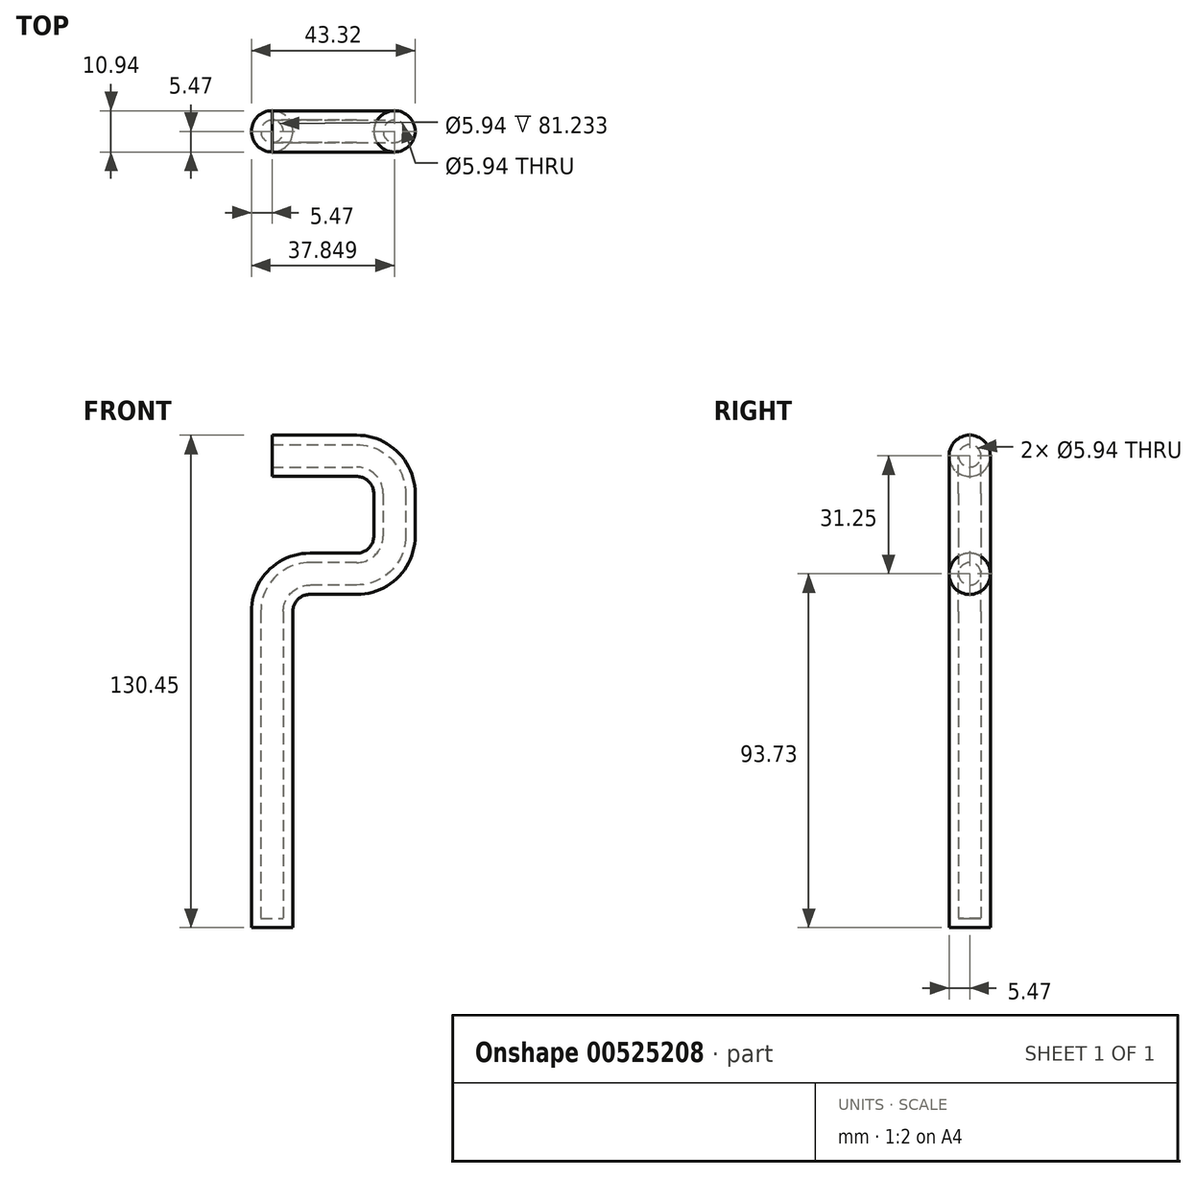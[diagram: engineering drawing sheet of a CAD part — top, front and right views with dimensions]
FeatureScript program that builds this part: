
annotation { "Feature Type Name" : "Feature", "Feature Type Description" : "" }
export const myFeature = defineFeature(function(context is Context, id is Id, definition is map)
    precondition{}
    {
        {
            var Q0;
            Q0=qCreatedBy(makeId("Front.planeOp"),FACE);
            var sketch = newSketch(context, id + "F0", { "sketchPlane" : qUnion([Q0])});
            skLineSegment(sketch, "E0", {"start": v(0, 0) * mm, "end": v(22.38, 0) * mm});
            skLineSegment(sketch, "E1", {"start": v(32.38, -10) * mm, "end": v(32.38, -21.25) * mm});
            skLineSegment(sketch, "E2", {"start": v(22.38, -31.25) * mm, "end": v(10, -31.25) * mm});
            skLineSegment(sketch, "E3", {"start": v(0, -124.98) * mm, "end": v(0, -41.25) * mm});
            skPoint(sketch, "E4.visualSharp", {"position": v(32.38, 0) * mm});
            skArc(sketch, "E4.filletArc", {"start": v(32.38, -10) * mm, "mid": v(29.45, -2.93) * mm, "end": v(22.38, 0) * mm});
            skPoint(sketch, "E5.visualSharp", {"position": v(32.38, -31.25) * mm});
            skArc(sketch, "E5.filletArc", {"start": v(22.38, -31.25) * mm, "mid": v(29.45, -28.32) * mm, "end": v(32.38, -21.25) * mm});
            skPoint(sketch, "E6.visualSharp", {"position": v(0, -31.25) * mm});
            skArc(sketch, "E6.filletArc", {"start": v(10, -31.25) * mm, "mid": v(2.93, -34.18) * mm, "end": v(0, -41.25) * mm});
            skSolve(sketch);
        }
        {
            var Q0;
            Q0=qCreatedBy(makeId("Right.planeOp"),FACE);
            var sketch = newSketch(context, id + "F1", { "sketchPlane" : qUnion([Q0])});
            skCircle(sketch, "E7", {"center": v(0, 0) * mm, "radius": 5.47 * mm});
            skSolve(sketch);
        }
        {
            var Q0;
            Q0=makeQuery(id+"F1.imprint","IMPRINT",FACE,{"disambiguationData":[TD([[makeQuery(id+"F1.imprint","IMPRINT",EDGE,{"derivedFrom":sQuery(id+"F1.wireOp",EDGE,"E7")}),1.0]])]});
            var Q1;
            Q1=sQuery(id+"F0.wireOp",EDGE,"E0");
            var Q2;
            Q2=sQuery(id+"F0.wireOp",EDGE,"E4.filletArc");
            var Q3;
            Q3=sQuery(id+"F0.wireOp",EDGE,"E1");
            var Q4;
            Q4=sQuery(id+"F0.wireOp",EDGE,"E5.filletArc");
            var Q5;
            Q5=sQuery(id+"F0.wireOp",EDGE,"E2");
            var Q6;
            Q6=sQuery(id+"F0.wireOp",EDGE,"E6.filletArc");
            var Q7;
            Q7=sQuery(id+"F0.wireOp",EDGE,"E3");
            sweep(context, id + "F2", {"profiles" : qUnion([Q0]), "path" : qUnion([Q1, Q2, Q3, Q4, Q5, Q6, Q7])});
        }
        {
            var Q0;
            Q0=makeQuery(id+"F2.opSweep","CAP_FACE",FACE,{"disambiguationData":[OSD([sQuery(id+"F0.wireOp",VERTEX,"E0.start"),sQuery(id+"F1.wireOp",EDGE,"E7")])],"isStart":true});
            shell(context, id + "F3", {"entities" : qUnion([Q0]), "thickness" : 2.5 * mm});
        }
    });
